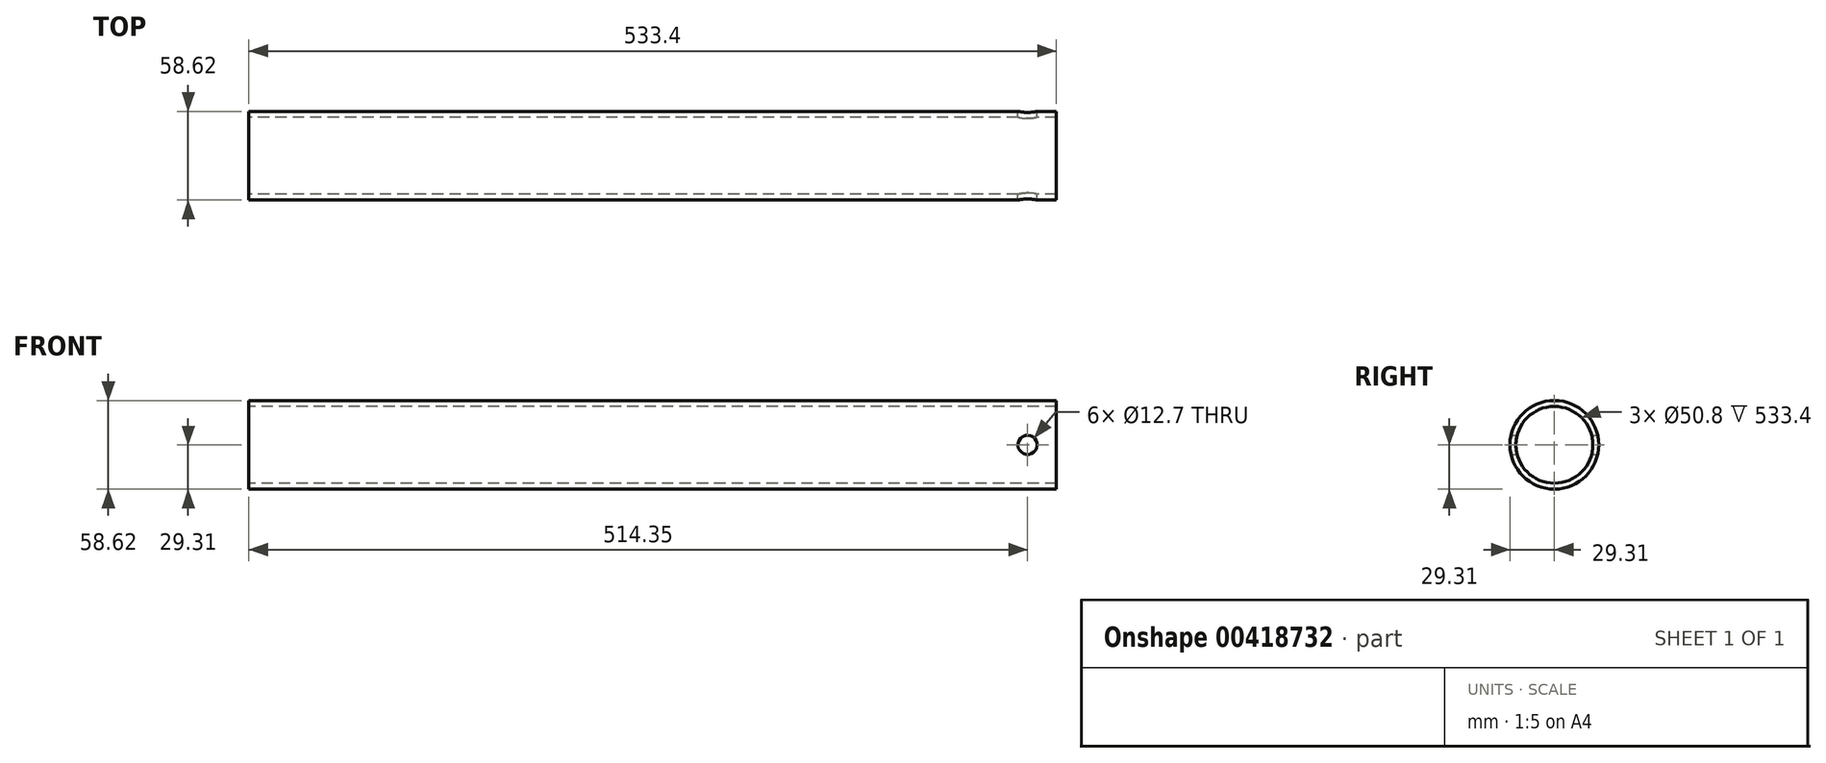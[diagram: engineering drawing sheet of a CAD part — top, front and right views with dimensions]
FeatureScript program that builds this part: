
annotation { "Feature Type Name" : "Feature", "Feature Type Description" : "" }
export const myFeature = defineFeature(function(context is Context, id is Id, definition is map)
    precondition{}
    {
        {
            var Q0;
            Q0=qCreatedBy(makeId("Right.planeOp"),FACE);
            var sketch = newSketch(context, id + "F0", { "sketchPlane" : qUnion([Q0])});
            skCircle(sketch, "E0", {"center": v(0, 0) * mm, "radius": 25.4 * mm});
            skCircle(sketch, "E1.0", {"center": v(0, 0) * mm, "radius": 29.31 * mm});
            skSolve(sketch);
        }
        {
            var Q0;
            Q0=makeQuery(id+"F0.imprint","IMPRINT",FACE,{"disambiguationData":[TD([[makeQuery(id+"F0.imprint","IMPRINT",EDGE,{"derivedFrom":sQuery(id+"F0.wireOp",EDGE,"E0")}),-1.0]])]});
            extrude(context, id + "F1", {"entities" : qUnion([Q0]), "endBound" : BoundingType.SYMMETRIC, "depth" : 533.4 * mm});
        }
        {
            var Q0;
            Q0=qCreatedBy(makeId("Front.planeOp"),FACE);
            var sketch = newSketch(context, id + "F2", { "sketchPlane" : qUnion([Q0])});
            skCircle(sketch, "E2", {"center": v(247.65, 0) * mm, "radius": 6.35 * mm});
            skLineSegment(sketch, "E3.0", {"start": v(266.7, 29.31) * mm, "end": v(266.7, -29.31) * mm});
            skLineSegment(sketch, "E4", {"start": v(266.7, 0) * mm, "end": v(247.65, 0) * mm, "construction": true});
            skSolve(sketch);
        }
        {
            var Q0;
            Q0=makeQuery(id+"F2.imprint","IMPRINT",FACE,{"disambiguationData":[TD([[makeQuery(id+"F2.imprint","IMPRINT",EDGE,{"derivedFrom":sQuery(id+"F2.wireOp",EDGE,"E2")}),1.0]])]});
            extrude(context, id + "F3", {"entities" : qUnion([Q0]), "operationType" : NewBodyOperationType.REMOVE, "endBound" : BoundingType.SYMMETRIC, "depth" : 76.2 * mm});
        }
    });
